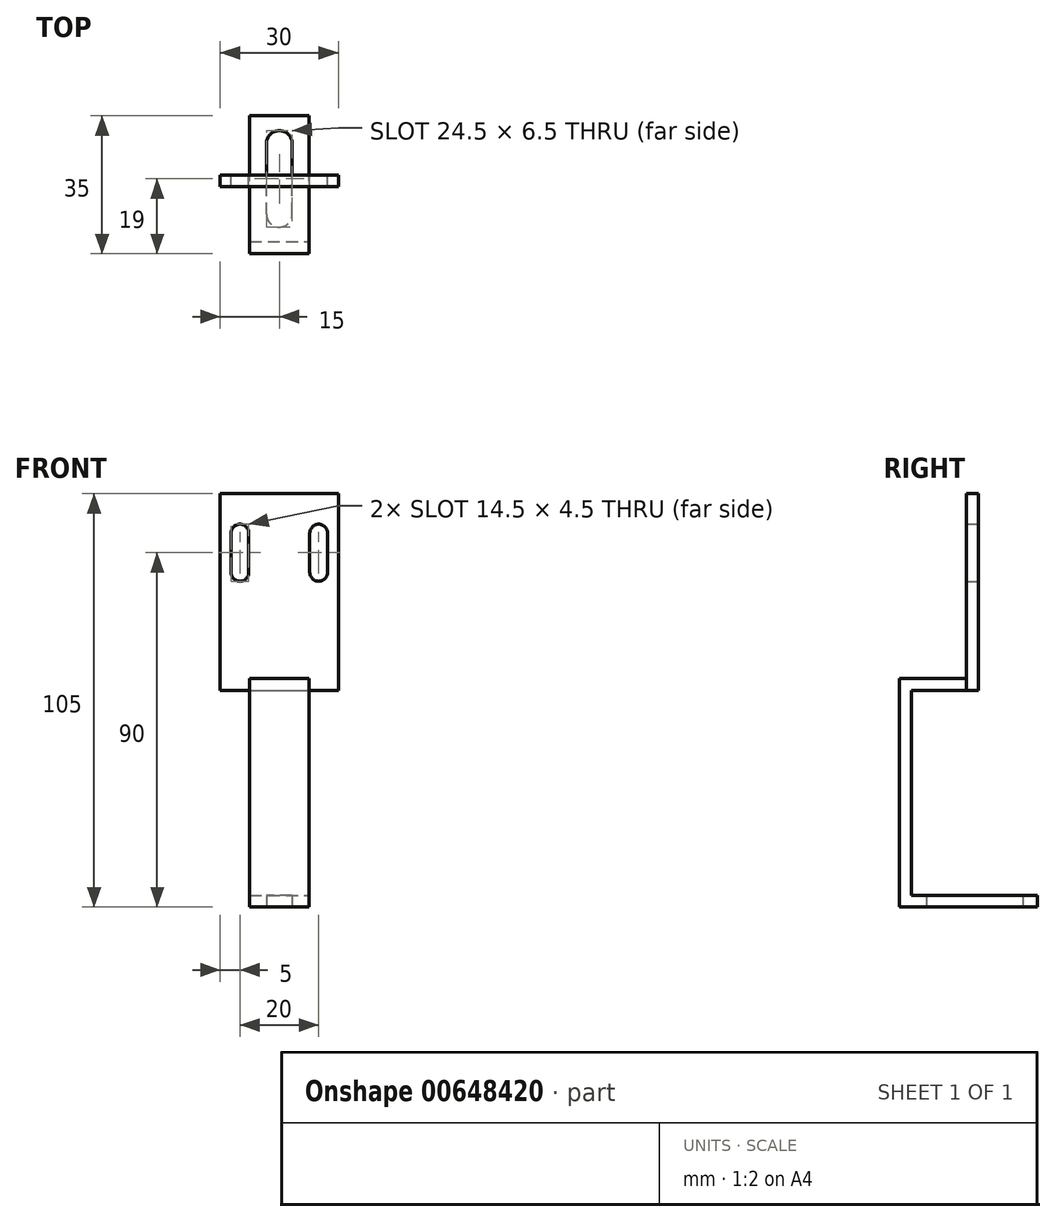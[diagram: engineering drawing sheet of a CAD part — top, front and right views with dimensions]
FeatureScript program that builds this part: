
annotation { "Feature Type Name" : "Feature", "Feature Type Description" : "" }
export const myFeature = defineFeature(function(context is Context, id is Id, definition is map)
    precondition{}
    {
        {
            var Q0;
            Q0=qCreatedBy(makeId("Front.planeOp"),FACE);
            var sketch = newSketch(context, id + "F0", { "sketchPlane" : qUnion([Q0])});
            skLineSegment(sketch, "E0.bottom", {"start": v(-15, 25) * mm, "end": v(15, 25) * mm});
            skLineSegment(sketch, "E0.top", {"start": v(-15, -25) * mm, "end": v(15, -25) * mm});
            skLineSegment(sketch, "E0.left", {"start": v(-15, 25) * mm, "end": v(-15, -25) * mm});
            skLineSegment(sketch, "E0.right", {"start": v(15, 25) * mm, "end": v(15, -25) * mm});
            skPoint(sketch, "E0.middle", {"position": v(0, 0) * mm});
            skArc(sketch, "E1", {"start": v(-7.75, 15) * mm, "mid": v(-10, 17.25) * mm, "end": v(-12.25, 15) * mm});
            skArc(sketch, "E2", {"start": v(-12.25, 5) * mm, "mid": v(-10, 2.75) * mm, "end": v(-7.75, 5) * mm});
            skLineSegment(sketch, "E3", {"start": v(-7.75, 15) * mm, "end": v(-7.75, 5) * mm});
            skLineSegment(sketch, "E4", {"start": v(-12.25, 15) * mm, "end": v(-12.25, 5) * mm});
            skArc(sketch, "E5.MirrorCS", {"start": v(12.25, 5) * mm, "mid": v(10, 2.75) * mm, "end": v(7.75, 5) * mm});
            skArc(sketch, "E6.MirrorCS", {"start": v(7.75, 15) * mm, "mid": v(10, 17.25) * mm, "end": v(12.25, 15) * mm});
            skLineSegment(sketch, "E7.MirrorCS", {"start": v(12.25, 15) * mm, "end": v(12.25, 5) * mm});
            skLineSegment(sketch, "E8.MirrorCS", {"start": v(7.75, 15) * mm, "end": v(7.75, 5) * mm});
            skSolve(sketch);
        }
        {
            var Q0;
            Q0 = qSketchRegion(id + "F0", true);
            extrude(context, id + "F1", {"entities" : qUnion([Q0]), "depth" : 3 * mm, "offsetDistance" : 25 * mm});
        }
        {
            var Q0;
            Q0=makeQuery(id+"F1.opExtrude","CAP_FACE",FACE,{"disambiguationData":[OSD([sQuery(id+"F0.wireOp",EDGE,"E0.bottom"),sQuery(id+"F0.wireOp",EDGE,"E0.top"),sQuery(id+"F0.wireOp",EDGE,"E0.left"),sQuery(id+"F0.wireOp",EDGE,"E0.right"),sQuery(id+"F0.wireOp",EDGE,"E1"),sQuery(id+"F0.wireOp",EDGE,"E2"),sQuery(id+"F0.wireOp",EDGE,"E3"),sQuery(id+"F0.wireOp",EDGE,"E4"),sQuery(id+"F0.wireOp",EDGE,"E5.MirrorCS"),sQuery(id+"F0.wireOp",EDGE,"E6.MirrorCS"),sQuery(id+"F0.wireOp",EDGE,"E7.MirrorCS"),sQuery(id+"F0.wireOp",EDGE,"E8.MirrorCS")])],"isStart":false});
            var sketch = newSketch(context, id + "F2", { "sketchPlane" : qUnion([Q0])});
            skLineSegment(sketch, "E9.bottom", {"start": v(-7.5, -25) * mm, "end": v(7.5, -25) * mm});
            skLineSegment(sketch, "E9.top", {"start": v(-7.5, -22) * mm, "end": v(7.5, -22) * mm});
            skLineSegment(sketch, "E9.left", {"start": v(-7.5, -25) * mm, "end": v(-7.5, -22) * mm});
            skLineSegment(sketch, "E9.right", {"start": v(7.5, -25) * mm, "end": v(7.5, -22) * mm});
            skSolve(sketch);
        }
        {
            var Q0;
            Q0 = qSketchRegion(id + "F2", true);
            extrude(context, id + "F3", {"entities" : qUnion([Q0]), "operationType" : NewBodyOperationType.ADD, "depth" : 17 * mm, "offsetDistance" : 25 * mm});
        }
        {
            var Q0;
            Q0=makeQuery(id+"F3.boolean.opBoolean","MERGE",FACE,{"derivedFrom":[makeQuery(id+"F1.opExtrude","SWEPT_FACE",FACE,{"disambiguationData":[OSD([sQuery(id+"F0.wireOp",EDGE,"E0.top")])]}),makeQuery(id+"F3.opExtrude","SWEPT_FACE",FACE,{"disambiguationData":[OSD([sQuery(id+"F2.wireOp",EDGE,"E9.bottom")])]})]});
            var sketch = newSketch(context, id + "F4", { "sketchPlane" : qUnion([Q0])});
            skLineSegment(sketch, "E10.bottom", {"start": v(-7.5, 20) * mm, "end": v(7.5, 20) * mm});
            skLineSegment(sketch, "E10.top", {"start": v(-7.5, 17) * mm, "end": v(7.5, 17) * mm});
            skLineSegment(sketch, "E10.left", {"start": v(-7.5, 20) * mm, "end": v(-7.5, 17) * mm});
            skLineSegment(sketch, "E10.right", {"start": v(7.5, 20) * mm, "end": v(7.5, 17) * mm});
            skSolve(sketch);
        }
        {
            var Q0;
            Q0 = qSketchRegion(id + "F4", true);
            extrude(context, id + "F5", {"entities" : qUnion([Q0]), "operationType" : NewBodyOperationType.ADD, "depth" : 55 * mm, "offsetDistance" : 25 * mm});
        }
        {
            var Q0;
            Q0=makeQuery(id+"F5.opExtrude","CAP_FACE",FACE,{"disambiguationData":[OSD([sQuery(id+"F4.wireOp",EDGE,"E10.bottom"),sQuery(id+"F4.wireOp",EDGE,"E10.top"),sQuery(id+"F4.wireOp",EDGE,"E10.left"),sQuery(id+"F4.wireOp",EDGE,"E10.right")])],"isStart":false});
            var sketch = newSketch(context, id + "F6", { "sketchPlane" : qUnion([Q0])});
            skLineSegment(sketch, "E11.bottom", {"start": v(-7.5, 20) * mm, "end": v(7.5, 20) * mm});
            skLineSegment(sketch, "E11.top", {"start": v(-7.5, -15) * mm, "end": v(7.5, -15) * mm});
            skLineSegment(sketch, "E11.left", {"start": v(-7.5, 20) * mm, "end": v(-7.5, -15) * mm});
            skLineSegment(sketch, "E11.right", {"start": v(7.5, 20) * mm, "end": v(7.5, -15) * mm});
            skArc(sketch, "E12", {"start": v(3.25, 10) * mm, "mid": v(0, 13.25) * mm, "end": v(-3.25, 10) * mm});
            skArc(sketch, "E13", {"start": v(-3.25, -8) * mm, "mid": v(0, -11.25) * mm, "end": v(3.25, -8) * mm});
            skLineSegment(sketch, "E14", {"start": v(3.25, 10) * mm, "end": v(3.25, -8) * mm});
            skLineSegment(sketch, "E15", {"start": v(-3.25, 10) * mm, "end": v(-3.25, -8) * mm});
            skSolve(sketch);
        }
        {
            var Q0;
            Q0 = qSketchRegion(id + "F6", true);
            extrude(context, id + "F7", {"entities" : qUnion([Q0]), "operationType" : NewBodyOperationType.ADD, "oppositeDirection" : true, "depth" : 3 * mm, "offsetDistance" : 25 * mm});
        }
    });
